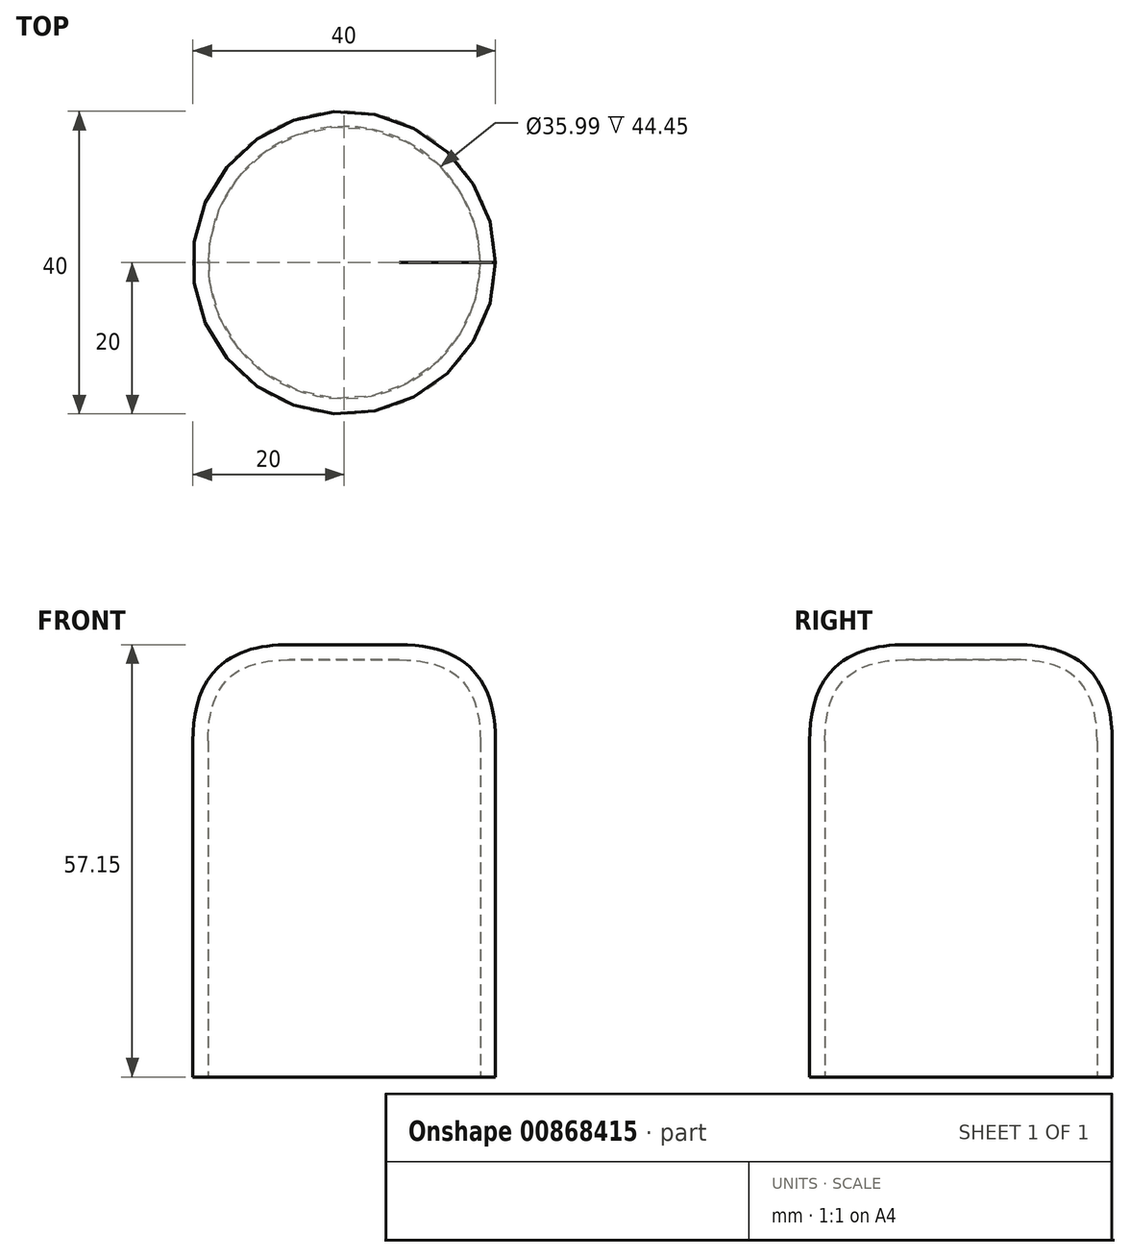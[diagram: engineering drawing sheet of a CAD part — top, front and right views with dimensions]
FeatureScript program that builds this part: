
annotation { "Feature Type Name" : "Feature", "Feature Type Description" : "" }
export const myFeature = defineFeature(function(context is Context, id is Id, definition is map)
    precondition{}
    {
        {
            var Q0;
            Q0=qCreatedBy(makeId("Top.planeOp"),FACE);
            var sketch = newSketch(context, id + "F0", { "sketchPlane" : qUnion([Q0])});
            skCircle(sketch, "E0", {"center": v(0, 0) * mm, "radius": 20 * mm});
            skSolve(sketch);
        }
        {
            var Q0;
            Q0=makeQuery(id+"F0.imprint","IMPRINT",FACE,{"disambiguationData":[TD([[makeQuery(id+"F0.imprint","IMPRINT",EDGE,{"derivedFrom":sQuery(id+"F0.wireOp",EDGE,"E0")}),1.0]])]});
            extrude(context, id + "F1", {"entities" : qUnion([Q0]), "depth" : 57.15 * mm, "offsetDistance" : 25.4 * mm});
        }
        {
            var Q0;
            Q0=makeQuery(id+"F1.opExtrude","CAP_FACE",FACE,{"disambiguationData":[OSD([sQuery(id+"F0.wireOp",EDGE,"E0")])],"isStart":false});
            fillet(context, id + "F2", {"entities" : qUnion([Q0]), "radius" : 12.7 * mm, "tangentPropagation" : true, "rho" : 0.5, "crossSection" : FilletCrossSection.CONIC, "allowEdgeOverflow" : false});
        }
        {
            var Q0;
            Q0=makeQuery(id+"F1.opExtrude","CAP_FACE",FACE,{"disambiguationData":[OSD([sQuery(id+"F0.wireOp",EDGE,"E0")])],"isStart":true});
            var Q1;
            Q1=makeQuery(id+"F1.opExtrude","SWEPT_BODY",BODY,{"disambiguationData":[OSD([sQuery(id+"F0.wireOp",EDGE,"E0")])]});
            shell(context, id + "F3", {"entities" : qUnion([Q0]), "parts" : qUnion([Q1]), "thickness" : 2 * mm});
        }
    });
